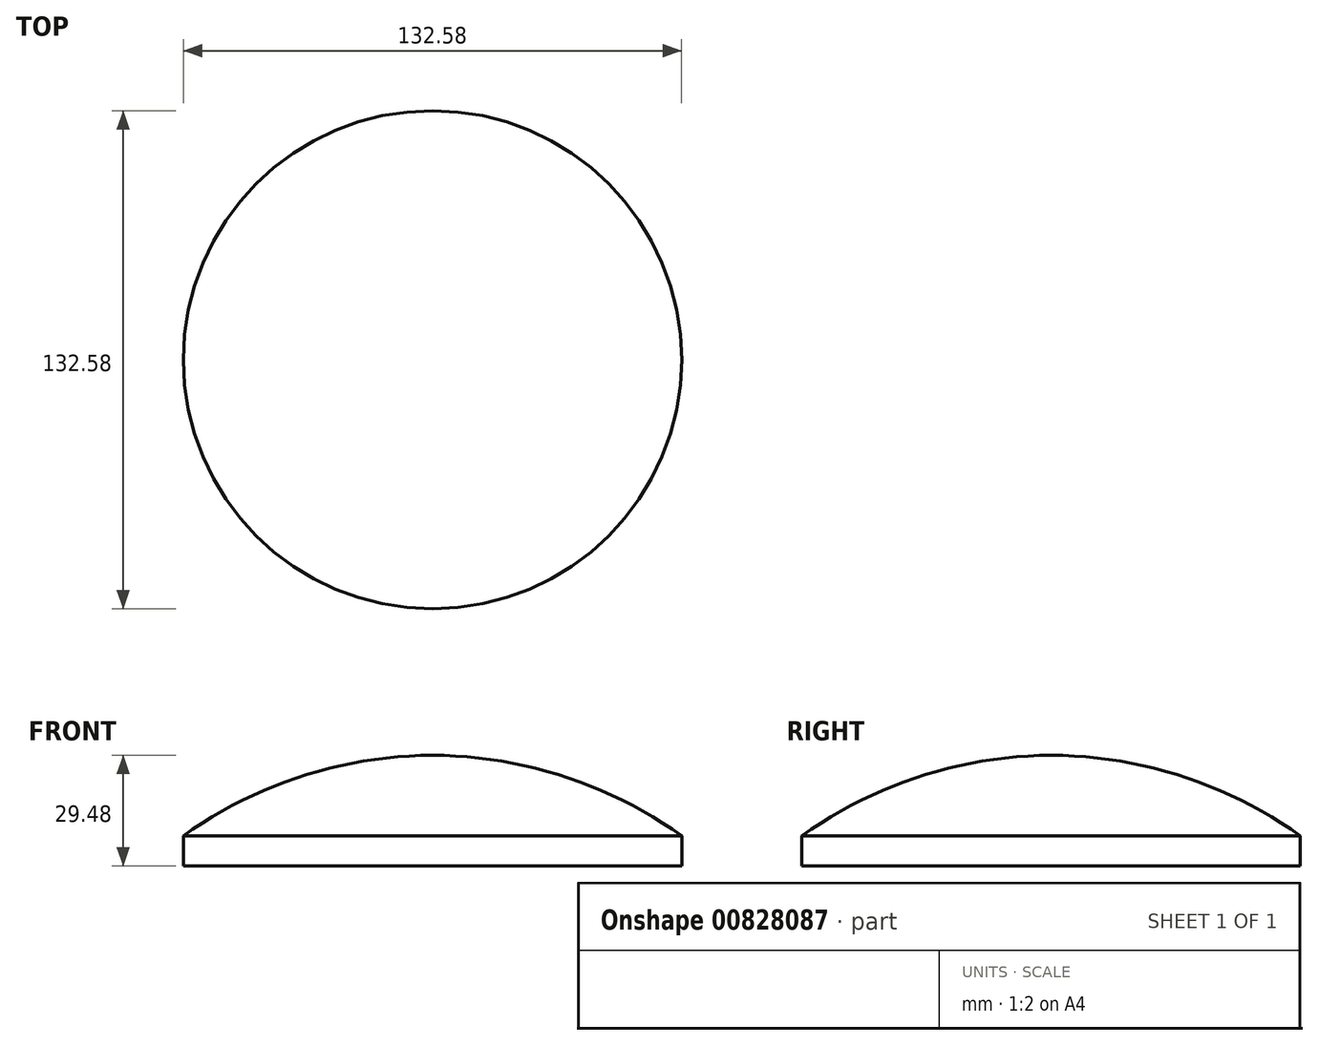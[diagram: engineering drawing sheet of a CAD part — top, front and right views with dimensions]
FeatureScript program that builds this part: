
annotation { "Feature Type Name" : "Feature", "Feature Type Description" : "" }
export const myFeature = defineFeature(function(context is Context, id is Id, definition is map)
    precondition{}
    {
        {
            var Q0;
            Q0=qCreatedBy(makeId("Front.planeOp"),FACE);
            var sketch = newSketch(context, id + "F0", { "sketchPlane" : qUnion([Q0])});
            skLineSegment(sketch, "E0.bottom", {"start": v(-66.3, 0) * mm, "end": v(0, 0) * mm});
            skLineSegment(sketch, "E0.left", {"start": v(-66.3, 0) * mm, "end": v(-66.3, 8.03) * mm});
            skArc(sketch, "E1", {"start": v(0, 29.48) * mm, "mid": v(-34.8, 23.89) * mm, "end": v(-66.3, 8.03) * mm});
            skPoint(sketch, "E0.right.end.orphan", {"position": v(0, 8.03) * mm});
            skLineSegment(sketch, "E2", {"start": v(0, 33.26) * mm, "end": v(0, -7.62) * mm, "construction": true});
            skLineSegment(sketch, "E3", {"start": v(0, 29.48) * mm, "end": v(0, 0) * mm});
            skSolve(sketch);
        }
        {
            var Q0;
            Q0=makeQuery(id+"F0.imprint","IMPRINT",FACE,{"disambiguationData":[TD([[makeQuery(id+"F0.imprint","IMPRINT",EDGE,{"derivedFrom":sQuery(id+"F0.wireOp",EDGE,"E0.bottom")}),1.0]])]});
            var Q1;
            Q1=sQuery(id+"F0.wireOp",EDGE,"E2");
            revolve(context, id + "F1", {"surfaceOperationType" : NewSurfaceOperationType.NEW, "entities" : qUnion([Q0]), "axis" : qUnion([Q1]), "revolveType" : RevolveType.FULL});
        }
    });
